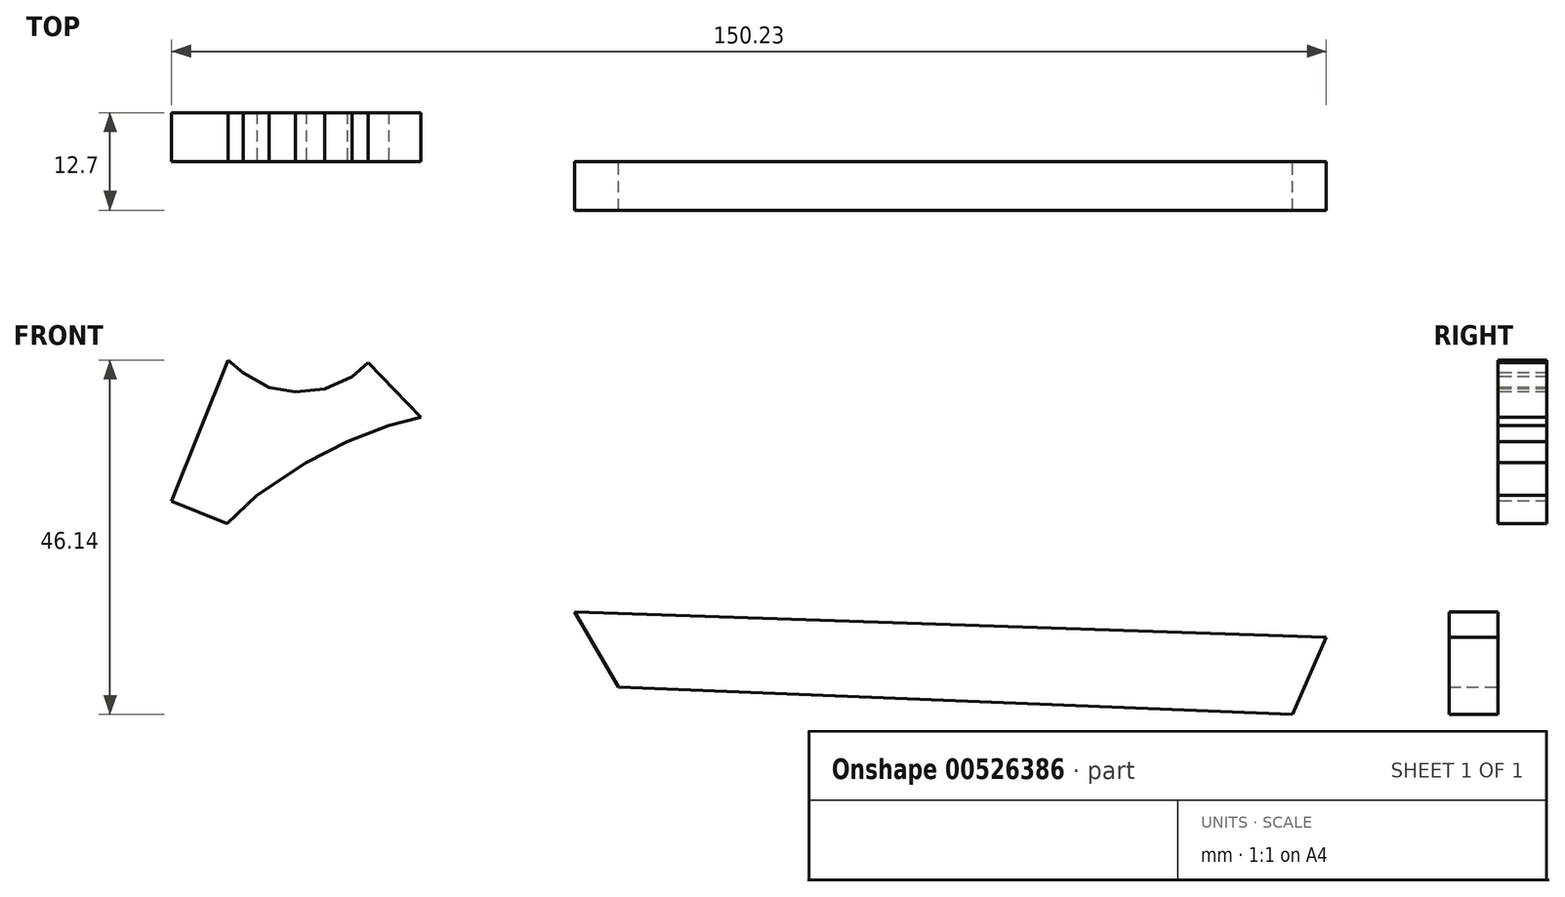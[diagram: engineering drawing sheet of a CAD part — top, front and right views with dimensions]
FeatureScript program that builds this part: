
annotation { "Feature Type Name" : "Feature", "Feature Type Description" : "" }
export const myFeature = defineFeature(function(context is Context, id is Id, definition is map)
    precondition{}
    {
        {
            var Q0;
            Q0=qCreatedBy(makeId("Front.planeOp"),FACE);
            var sketch = newSketch(context, id + "F0", { "sketchPlane" : qUnion([Q0])});
            skLineSegment(sketch, "E0", {"start": v(-110.13, 36.57) * mm, "end": v(-110.13, 0) * mm});
            skLineSegment(sketch, "E1", {"start": v(-110.13, 0) * mm, "end": v(-110.13, 0) * mm});
            skLineSegment(sketch, "E2", {"start": v(-103.68, 0) * mm, "end": v(-110.13, 0) * mm});
            skLineSegment(sketch, "E3", {"start": v(-45.08, 36.07) * mm, "end": v(-110.13, 36.57) * mm});
            skLineSegment(sketch, "E4", {"start": v(-50.92, 21.2) * mm, "end": v(-103.68, 0) * mm});
            skLineSegment(sketch, "E5", {"start": v(-45.08, 36.07) * mm, "end": v(-52.44, 17.7) * mm});
            skLineSegment(sketch, "E6", {"start": v(-52.44, 17.7) * mm, "end": v(-45.24, 14.8) * mm});
            skLineSegment(sketch, "E7", {"start": v(-45.08, 36.07) * mm, "end": v(-43.11, 34.39) * mm});
            skLineSegment(sketch, "E8", {"start": v(-39.77, 32.52) * mm, "end": v(-43.11, 34.39) * mm});
            skLineSegment(sketch, "E9", {"start": v(-36.33, 31.94) * mm, "end": v(-39.77, 32.52) * mm});
            skLineSegment(sketch, "E10", {"start": v(-32.55, 32.33) * mm, "end": v(-36.33, 31.94) * mm});
            skLineSegment(sketch, "E11", {"start": v(-32.55, 32.33) * mm, "end": v(-28.94, 33.89) * mm});
            skLineSegment(sketch, "E12", {"start": v(-28.94, 33.89) * mm, "end": v(-28.94, 33.89) * mm});
            skLineSegment(sketch, "E13", {"start": v(-26.86, 35.76) * mm, "end": v(-28.94, 33.89) * mm});
            skLineSegment(sketch, "E14", {"start": v(-126.2, 20.45) * mm, "end": v(-126.2, 20.45) * mm});
            skLineSegment(sketch, "E15", {"start": v(-45.24, 14.8) * mm, "end": v(-41.32, 18.5) * mm});
            skLineSegment(sketch, "E16", {"start": v(-41.32, 18.5) * mm, "end": v(-34.96, 22.74) * mm});
            skLineSegment(sketch, "E17", {"start": v(-34.96, 22.74) * mm, "end": v(-29.57, 25.42) * mm});
            skLineSegment(sketch, "E18", {"start": v(-29.57, 25.42) * mm, "end": v(-29.57, 25.42) * mm});
            skLineSegment(sketch, "E19", {"start": v(-24.21, 27.53) * mm, "end": v(-29.57, 25.42) * mm});
            skLineSegment(sketch, "E20", {"start": v(-24.21, 27.53) * mm, "end": v(-20.03, 28.62) * mm});
            skLineSegment(sketch, "E21", {"start": v(-26.86, 35.76) * mm, "end": v(-20.03, 28.62) * mm});
            skSolve(sketch);
        }
        {
            var Q0;
            Q0=makeQuery(id+"F0.imprint","IMPRINT",FACE,{"disambiguationData":[TD([[makeQuery(id+"F0.imprint","IMPRINT",EDGE,{"derivedFrom":sQuery(id+"F0.wireOp",EDGE,"E0")}),1.0]])]});
            var sketch = newSketch(context, id + "F1", { "sketchPlane" : qUnion([Q0])});
            skSolve(sketch);
        }
        {
            var Q0;
            Q0=makeQuery(id+"F1.imprint","IMPRINT",FACE,{"disambiguationData":[TD([[makeQuery(id+"F1.imprint","IMPRINT",EDGE,{"derivedFrom":makeQuery(id+"F0.imprint","IMPRINT",EDGE,{"derivedFrom":sQuery(id+"F0.wireOp",EDGE,"E0")})}),1.0]])]});
            var Q1;
            {var subQ3=sQuery(id+"F0.wireOp",EDGE,"E6");Q1=makeQuery(id+"F0.imprint","IMPRINT",FACE,{"disambiguationData":[TD([[makeQuery(id+"F0.imprint","IMPRINT",EDGE,{"derivedFrom":subQ3}),1.0]])]});}
            extrude(context, id + "F2", {"entities" : qUnion([Q0, Q1]), "oppositeDirection" : true, "depth" : 6.35 * mm, "offsetDistance" : 25.4 * mm});
        }
        {
            var Q0;
            Q0=qCreatedBy(makeId("Front.planeOp"),FACE);
            var sketch = newSketch(context, id + "F3", { "sketchPlane" : qUnion([Q0])});
            skLineSegment(sketch, "E22", {"start": v(0, 3.28) * mm, "end": v(97.8, 0) * mm});
            skLineSegment(sketch, "E23", {"start": v(0, 3.28) * mm, "end": v(5.68, -6.46) * mm});
            skLineSegment(sketch, "E24", {"start": v(5.68, -6.46) * mm, "end": v(93.37, -10.07) * mm});
            skLineSegment(sketch, "E25", {"start": v(93.37, -10.07) * mm, "end": v(93.37, -10.07) * mm});
            skLineSegment(sketch, "E26", {"start": v(93.37, -10.07) * mm, "end": v(97.8, 0) * mm});
            skSolve(sketch);
        }
        {
            var Q0;
            Q0 = qSketchRegion(id + "F3", true);
            extrude(context, id + "F4", {"entities" : qUnion([Q0]), "depth" : 6.35 * mm, "offsetDistance" : 25.4 * mm});
        }
    });
